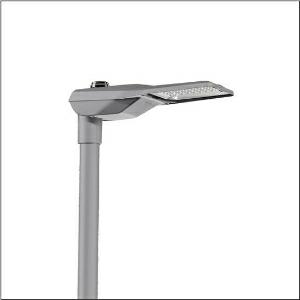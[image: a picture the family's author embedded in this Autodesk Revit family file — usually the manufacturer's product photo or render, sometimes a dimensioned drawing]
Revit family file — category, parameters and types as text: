
# Revit family: streetlight_sl_21_mini___p0_8a_5xe6u27n08gb_261a
name_source: partatom
category: Lighting Fixtures
units: mm (PartAtom-declared; Revit-internal decimal feet)

## family parameters
Cut with Voids When Loaded = No
Host = Face
Light Source = No
Part Type = Normal
Room Calculation Point = No
Round Connector Dimension = Use Diameter
Shared = No

## types (1)
- --- (1 x LED, 4960 lm, 40.4 W, 2200K)
    Apparent Load = 40 VA
    CIE Flux Codes = 33 69 96 100 100
    Color Rendering = 70
    Color Temperature = 2200K
    Default Elevation = 1800 mm
    Description = Streetlight SL 21 mini, mast luminaire, primary light control with lens, of PMMA, primary optical cover: cover, of toughened safety glass, transparent, light distribution: P0.8a, light emission: direct distribution, primary light characteristic: asymmetric, installation type: side-entry, LED, 3G 1.5mm², High Power LED, rated luminous flux: 4.960lm, luminous efficacy: 123lm/W, light colour: 722, colour temperature: 2200K, control gear: NEMA (7pin), control: flexible luminous flux parameterisation, time-dependent luminous flux control, constant luminous flux control, pre-setting: linear dimming characteristic, overheat protection, mains connection: 230..240V, AC, 50/60Hz, connection cable pre-assembled, cable length: 8,5m, wiring characteristics: H07RN-F, start of lifetime: 40W, end of service life: 41W, reduction: 19W, luminaire housing, of diecast aluminium (EN AC-44300), powder-coated, SITECO metallic grey (DB 702S), corrosivity category C5 high according to DIN EN ISO 12944, multi-level sealing system, sealing non-destructively replaceable, inclination adjustable: 0°, 5°, 10°, 15°, length: 628mm, width: 235mm, height: 110mm, spigot size: 42mm (side-entry), mounting height: 4..8m, protection rating (complete): IP66, insulation class (complete): insulation class I (protective earthing), certification: CE, ENEC, ENEC+, VDE, impact resistance: IK10, permissible operating ambient temperature for outdoor applications: -40..+50°C, standard-compliant lighting for roads and squares, packaging unit: 1 piece

Light Distribution: P0.8a
    Height = 110 mm
    Lamp = 1 x LED
    Lamp Light Flux = 4960 lm
    Lamp Power = 40.4 W
    Lamp count = 1
    Length = 625 mm
    Luminous efficacy = 123 lm/W
    Manufacturer = Siteco
    ModVariant = No
    Model = 5XE6U27N08GB
    Number of Poles = 1
    OnlyDefault = Yes
    Power Factor = 1
    Product Name = Streetlight SL 21 mini | P0.8a
    Product group = mast luminaire | pylon top
    ProductGroupID = 6100
    Protection Class = Protection class I
    Protection Degree = IP 66
    RLX_Detail_Level = 1
    RLX_Emergency_Light_Flux = 0 lm
    RLX_Emergency_Type = 0
    RLX_Emergency_Type_DB = No
    RlxData = <blob elided: 91637 chars, md5=6caf8eae>
    Socket = socket
    Standby Power = 0 W
    System Light Flux = 4960 lm
    System Power = 40 W
    Type Comments = factory setting: luminous flux: 100 % | dim-lin: 254 | 812 mA
    Type Image = l_1294379.jpg
    URL = http://relux.com
    VarID = @adj_081363
    Voltage = 0 V
    Weight = 0.00 kg
    Width = 234 mm

## geometry (parser evidence)
native form markers: Blend x4, Sweep x10
no freeform markers — native parametric forms only
